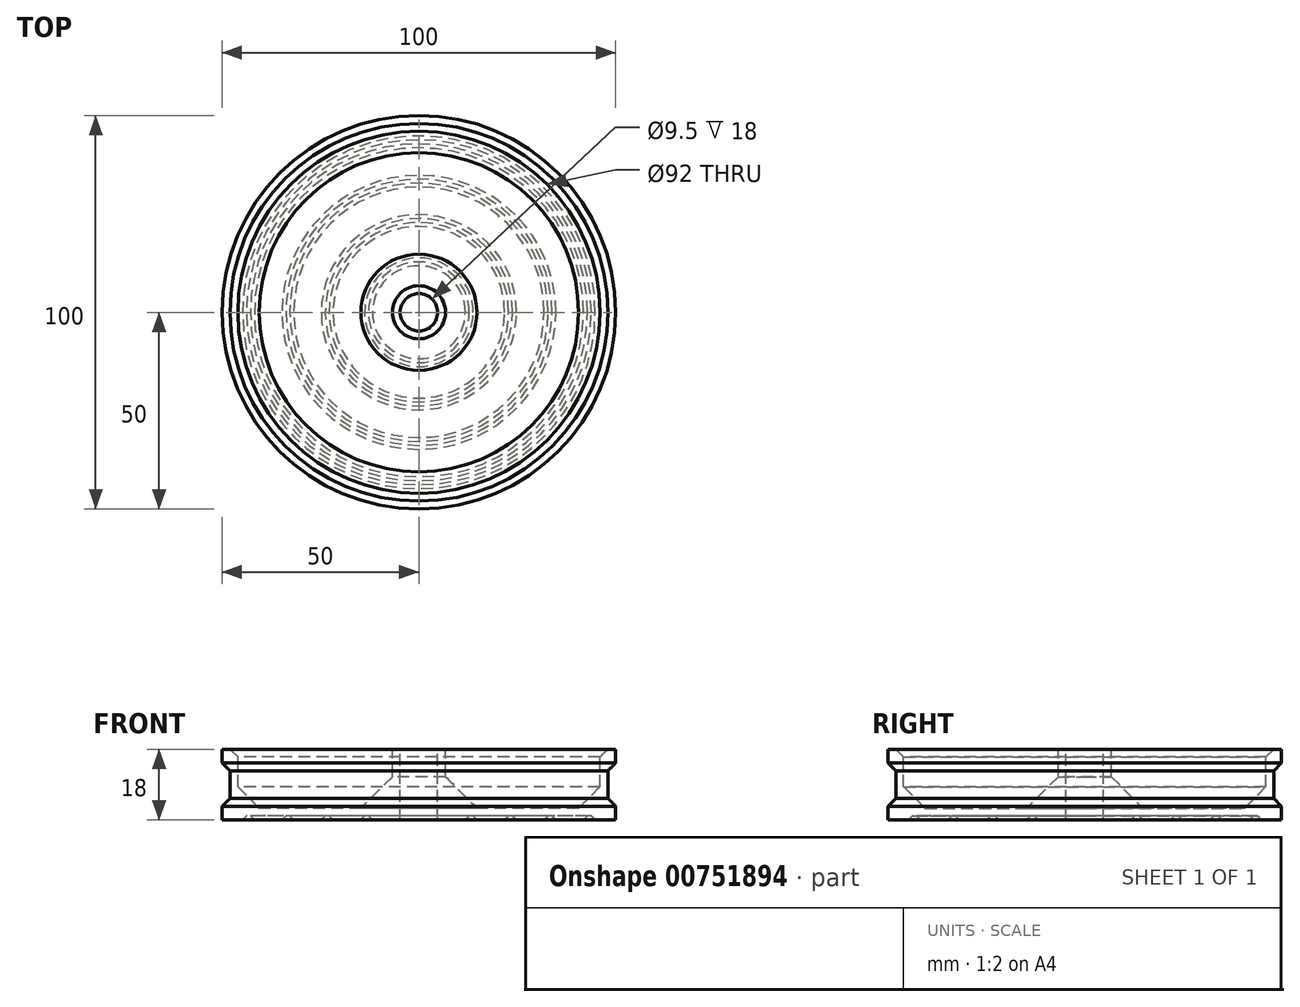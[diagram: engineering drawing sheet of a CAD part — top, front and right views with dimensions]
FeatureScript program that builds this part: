
annotation { "Feature Type Name" : "Feature", "Feature Type Description" : "" }
export const myFeature = defineFeature(function(context is Context, id is Id, definition is map)
    precondition{}
    {
        {
            var Q0;
            Q0=qCreatedBy(makeId("Front.planeOp"),FACE);
            var sketch = newSketch(context, id + "F0", { "sketchPlane" : qUnion([Q0])});
            skLineSegment(sketch, "E0", {"start": v(0, 9) * mm, "end": v(-6.75, 9) * mm});
            skLineSegment(sketch, "E1", {"start": v(-50, 9) * mm, "end": v(-50, 5.5) * mm});
            skLineSegment(sketch, "E2", {"start": v(-50, 5.5) * mm, "end": v(-48, 3.5) * mm});
            skLineSegment(sketch, "E3", {"start": v(-48, 3.5) * mm, "end": v(-48, 0) * mm});
            skLineSegment(sketch, "E4.MirrorCS", {"start": v(0, -9) * mm, "end": v(-11.8, -9) * mm});
            skLineSegment(sketch, "E5.MirrorCS", {"start": v(-48, -3.5) * mm, "end": v(-48, 0) * mm});
            skLineSegment(sketch, "E6.MirrorCS", {"start": v(-50, -5.5) * mm, "end": v(-48, -3.5) * mm});
            skLineSegment(sketch, "E7.MirrorCS", {"start": v(-50, -9) * mm, "end": v(-50, -5.5) * mm});
            skLineSegment(sketch, "E8", {"start": v(0, 9) * mm, "end": v(0, -9) * mm});
            skLineSegment(sketch, "E9", {"start": v(-6.75, 9) * mm, "end": v(-6.75, 2) * mm});
            skLineSegment(sketch, "E10", {"start": v(-48, 9) * mm, "end": v(-46, 7) * mm});
            skLineSegment(sketch, "E11", {"start": v(-46, 7) * mm, "end": v(-46, -0.56) * mm});
            skLineSegment(sketch, "E12", {"start": v(-46, -0.56) * mm, "end": v(-40.56, -6) * mm});
            skLineSegment(sketch, "E13", {"start": v(-40.56, -6) * mm, "end": v(-14.75, -6) * mm});
            skLineSegment(sketch, "E14", {"start": v(-14.75, -6) * mm, "end": v(-6.75, 2) * mm});
            skPoint(sketch, "E15.orphan", {"position": v(-6.5, -6) * mm});
            skLineSegment(sketch, "E16.trimOffspring", {"start": v(-48, 9) * mm, "end": v(-50, 9) * mm});
            skLineSegment(sketch, "E17", {"start": v(-44.8, -9) * mm, "end": v(-43.8, -8) * mm});
            skLineSegment(sketch, "E18", {"start": v(-43.8, -8) * mm, "end": v(-42.8, -8) * mm});
            skLineSegment(sketch, "E19", {"start": v(-42.8, -8) * mm, "end": v(-41.8, -9) * mm});
            skLineSegment(sketch, "E20.1.0.0", {"start": v(-33.8, -8) * mm, "end": v(-32.8, -8) * mm});
            skLineSegment(sketch, "E20.1.0.1", {"start": v(-34.8, -9) * mm, "end": v(-33.8, -8) * mm});
            skLineSegment(sketch, "E20.1.0.2", {"start": v(-32.8, -8) * mm, "end": v(-31.8, -9) * mm});
            skLineSegment(sketch, "E20.2.0.0", {"start": v(-23.8, -8) * mm, "end": v(-22.8, -8) * mm});
            skLineSegment(sketch, "E20.2.0.1", {"start": v(-24.8, -9) * mm, "end": v(-23.8, -8) * mm});
            skLineSegment(sketch, "E20.2.0.2", {"start": v(-22.8, -8) * mm, "end": v(-21.8, -9) * mm});
            skLineSegment(sketch, "E20.direction1", {"start": v(-41.8, -9) * mm, "end": v(-34.8, -9) * mm, "construction": true});
            skLineSegment(sketch, "E21.0.3.0", {"start": v(-13.8, -8) * mm, "end": v(-12.8, -8) * mm});
            skLineSegment(sketch, "E21.3.3.0", {"start": v(-14.8, -9) * mm, "end": v(-13.8, -8) * mm});
            skLineSegment(sketch, "E21.6.3.0", {"start": v(-12.8, -8) * mm, "end": v(-11.8, -9) * mm});
            skLineSegment(sketch, "E22.trimOffspring", {"start": v(-34.8, -9) * mm, "end": v(-41.8, -9) * mm});
            skLineSegment(sketch, "E23.trimOffspring", {"start": v(-24.8, -9) * mm, "end": v(-31.8, -9) * mm});
            skLineSegment(sketch, "E24.trimOffspring", {"start": v(-44.8, -9) * mm, "end": v(-50, -9) * mm});
            skLineSegment(sketch, "E25", {"start": v(-21.8, -9) * mm, "end": v(-14.8, -9) * mm});
            skLineSegment(sketch, "E26", {"start": v(-4.75, 9) * mm, "end": v(-4.75, -9) * mm});
            skSolve(sketch);
        }
        {
            var Q0;
            {var subQ0=sQuery(id+"F0.wireOp",EDGE,"E1");Q0=makeQuery(id+"F0.imprint","IMPRINT",FACE,{"disambiguationData":[TD([[makeQuery(id+"F0.imprint","IMPRINT",EDGE,{"derivedFrom":subQ0}),1.0]])]});}
            var Q1;
            Q1=sQuery(id+"F0.wireOp",EDGE,"E8");
            revolve(context, id + "F1", {"surfaceOperationType" : NewSurfaceOperationType.NEW, "entities" : qUnion([Q0]), "axis" : qUnion([Q1]), "revolveType" : RevolveType.FULL});
        }
    });
